# Revit family: Profilschiene gelocht_Schlitzweite 22mm
name_source: partatom
category: Generic Models
revit_build: Autodesk Revit 2015 (Build: 20140606_1530(x64)
units: mm (PartAtom-declared; Revit-internal decimal feet)

## types (32) — shared parameters
Manufacturer = OBO Bettermann
Material = Steel, Galvanized
URL = http://www.obo-bettermann.com

## per-type parameters (varying)
| type | Article Type | GTIN | Lenght | Manufacturer Art.No. | Material Thickness |
| MSL4141P3000FS | MSL4141P3000FS | 4012195698159 | 3000 mm  [stored 9.84252 ft] | 1122972 | 2 mm  [stored 0.00656168 ft] |
| MSL4141P1000FS | MSL4141P1000FS | 4012195698142 | 1000 mm  [stored 3.28084 ft] | 1122970 | 2 mm  [stored 0.00656168 ft] |
| MSL4141P6000FS | MSL4141P6000FS | 4012195698166 | 6000 mm  [stored 19.685 ft] | 1122974 | 2 mm  [stored 0.00656168 ft] |
| MSL4141PP1000FS | MSL4141PP1000FS | 4012195697923 | 1000 mm  [stored 3.28084 ft] | 1123008 | 2 mm  [stored 0.00656168 ft] |
| MSL4141PP3000FS | MSL4141PP3000FS | 4012195698319 | 3000 mm  [stored 9.84252 ft] | 1123010 | 2 mm  [stored 0.00656168 ft] |
| MSL4141PP6000FS | MSL4141PP6000FS | 4012195698326 | 6000 mm  [stored 19.685 ft] | 1123012 | 2 mm  [stored 0.00656168 ft] |
| MSL4141P1000FT | MSL4141P1000FT | 4012195698081 | 1000 mm  [stored 3.28084 ft] | 1122962 | 2 mm  [stored 0.00656168 ft] |
| MSL4141P3000FT | MSL4141P3000FT | 4012195698098 | 3000 mm  [stored 9.84252 ft] | 1122964 | 2 mm  [stored 0.00656168 ft] |
| MSL4141P6000FT | MSL4141P6000FT | 4012195698104 | 6000 mm  [stored 19.685 ft] | 1122966 | 2 mm  [stored 0.00656168 ft] |
| MSL4141PP1000FT | MSL4141PP1000FT | 4012195697862 | 1000 mm  [stored 3.28084 ft] | 1123001 | 2 mm  [stored 0.00656168 ft] |
| MSL4141PP3000FT | MSL4141PP3000FT | 4012195697909 | 3000 mm  [stored 9.84252 ft] | 1123003 | 2 mm  [stored 0.00656168 ft] |
| MSL4141PP6000FT | MSL4141PP6000FT | 4012195697916 | 6000 mm  [stored 19.685 ft] | 1123005 | 3 mm  [stored 0.00984252 ft] |
| MS4141P1000FS | MS4141P1000FS | 4012195697503 | 1000 mm  [stored 3.28084 ft] | 1122908 | 3 mm  [stored 0.00984252 ft] |
| MS4141P3000FS | MS4141P3000FS | 4012195686224 | 3000 mm  [stored 9.84252 ft] | 1122910 | 3 mm  [stored 0.00984252 ft] |
| MS4141P6000FS | MS4141P6000FS | 4012195686231 | 6000 mm  [stored 19.685 ft] | 1122912 | 3 mm  [stored 0.00984252 ft] |
| MS4141P1000FT | MS4141P1000FT | 4012195487272 | 1000 mm  [stored 3.28084 ft] | 1122606 | 3 mm  [stored 0.00984252 ft] |
| MS4141P3000FT | MS4141P3000FT | 4012195487876 | 1000 mm  [stored 3.28084 ft] | 1122622 | 3 mm  [stored 0.00984252 ft] |
| MS4141P6000FT | MS4141P6000FT | 4012195488170 | 6000 mm  [stored 19.685 ft] | 1122657 | 3 mm  [stored 0.00984252 ft] |
| MS4141PP1000FS | MS4141PP1000FT | 4012195697978 | 1000 mm  [stored 3.28084 ft] | 1122481 | 3 mm  [stored 0.00984252 ft] |
| MS4141PP3000FS | MS4141PP3000FT | 4012195686248 | 3000 mm  [stored 9.84252 ft] | 1122914 | 3 mm  [stored 0.00984252 ft] |
| MS4141PP6000FS | MS4141PP6000FT | 4012195686255 | 6000 mm  [stored 19.685 ft] | 1122916 | 3 mm  [stored 0.00984252 ft] |
| MS4141PP1000FT | MS4141PP1000FT | 4012195697961 | 1000 mm  [stored 3.28084 ft] | 1122479 | 3 mm  [stored 0.00984252 ft] |
| MS4141PP3000FT | MS4141PP3000FT | 4012195050735 | 3000 mm  [stored 9.84252 ft] | 1122483 | 3 mm  [stored 0.00984252 ft] |
| MS4141PP6000FT | MS4141PP6000FT | 4012195050742 | 6000 mm  [stored 19.685 ft] | 1122487 | 3 mm  [stored 0.00984252 ft] |
| MS4141P0200FT | MS4141P0200FT | 4012195484516 | 200 mm  [stored 0.656168 ft] | 1122509 | 3 mm  [stored 0.00984252 ft] |
| MS4141P0300FT | MS4141P0300FT | 4012195485896 | 300 mm | 1122517 | 3 mm  [stored 0.00984252 ft] |
| MS4141P0400FT | MS4141P0400FT | 4012195486251 | 400 mm  [stored 1.31234 ft] | 1122525 | 3 mm  [stored 0.00984252 ft] |
| MS4141P0500FT | MS4141P0500FT | 4012195486794 | 500 mm  [stored 1.64042 ft] | 1122533 | 3 mm  [stored 0.00984252 ft] |
| MS4141P0600FT | MS4141P0600FT | 4012195486916 | 600 mm | 1122541 | 3 mm  [stored 0.00984252 ft] |
| MS4141P0700FT | MS4141P0700FT | 4012195487036 | 700 mm  [stored 2.29659 ft] | 1122568 | 3 mm  [stored 0.00984252 ft] |
| MS4141P0800FT | MS4141P0800FT | 4012195487098 | 800 mm  [stored 2.62467 ft] | 1122576 | 3 mm  [stored 0.00984252 ft] |
| MS4141P0900FT | MS4141P0900FT | 4012195487159 | 900 mm  [stored 2.95276 ft] | 1122584 | 3 mm  [stored 0.00984252 ft] |

note: [stored X ft] marks values corroborated as IEEE doubles in the binary element streams (Revit-internal decimal feet)

## geometry (parser evidence)
native form markers: Sweep x5
no freeform markers — native parametric forms only
